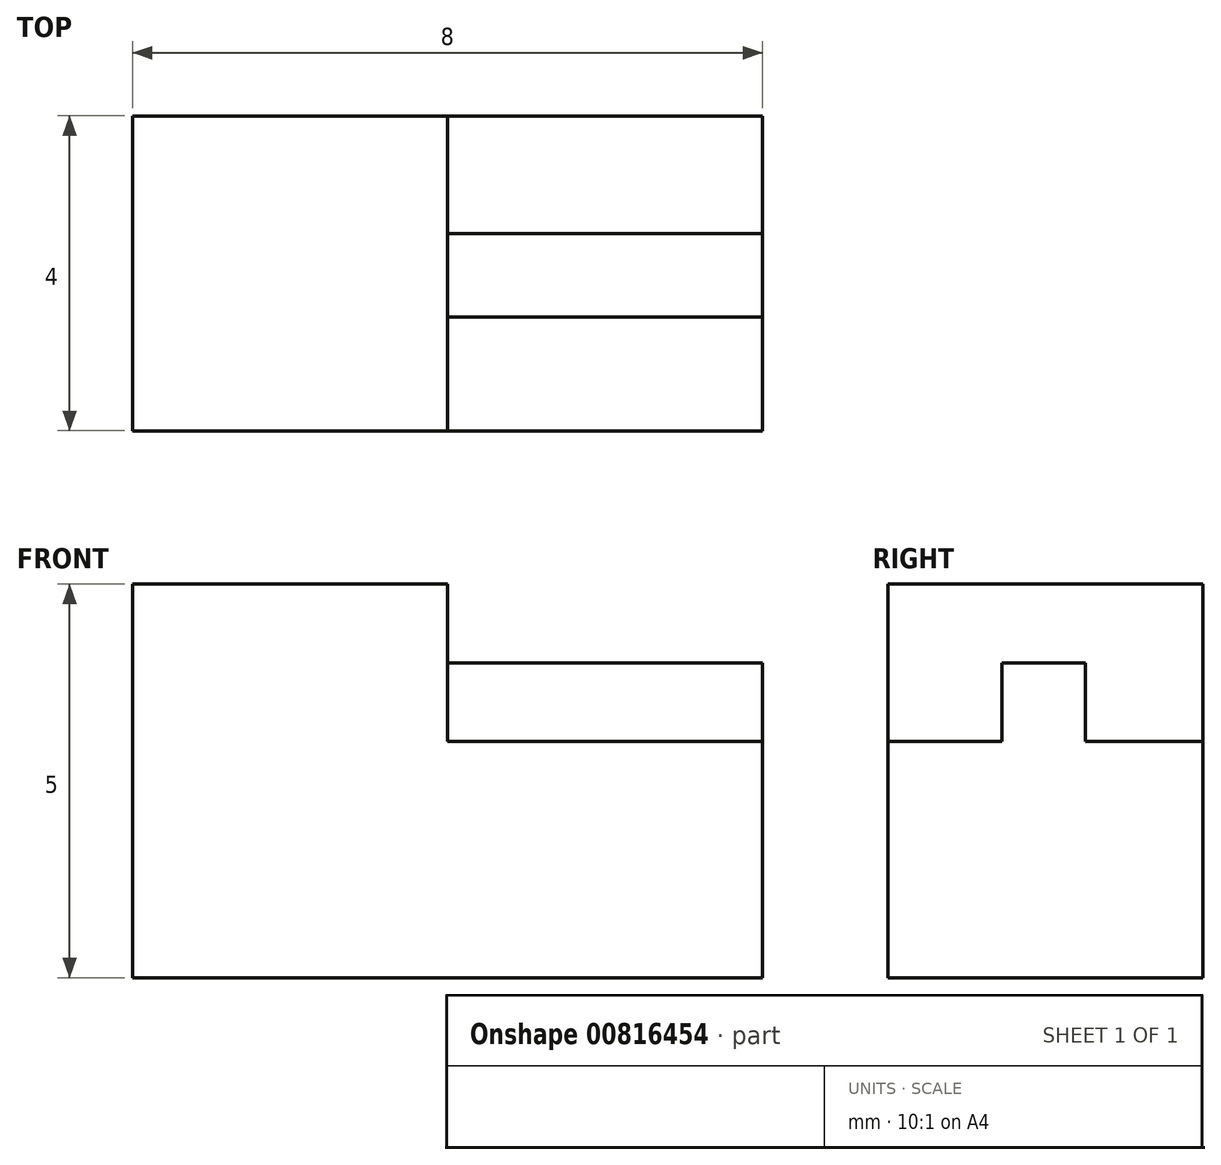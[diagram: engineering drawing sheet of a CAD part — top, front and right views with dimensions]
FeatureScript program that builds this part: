
annotation { "Feature Type Name" : "Feature", "Feature Type Description" : "" }
export const myFeature = defineFeature(function(context is Context, id is Id, definition is map)
    precondition{}
    {
        {
            var Q0;
            Q0=qCreatedBy(makeId("Top.planeOp"),FACE);
            var sketch = newSketch(context, id + "F0", { "sketchPlane" : qUnion([Q0])});
            skLineSegment(sketch, "E0.bottom", {"start": v(-16.71, -4.14) * mm, "end": v(-8.71, -4.14) * mm});
            skLineSegment(sketch, "E0.top", {"start": v(-16.71, -8.14) * mm, "end": v(-8.71, -8.14) * mm});
            skLineSegment(sketch, "E0.left", {"start": v(-16.71, -4.14) * mm, "end": v(-16.71, -8.14) * mm});
            skLineSegment(sketch, "E0.right", {"start": v(-8.71, -4.14) * mm, "end": v(-8.71, -8.14) * mm});
            skPoint(sketch, "E1.visualSharp", {"position": v(-16.71, -4.14) * mm});
            skLineSegment(sketch, "E1.filletArc", {"start": v(-16.71, -4.14) * mm, "end": v(-16.71, -4.14) * mm});
            skPoint(sketch, "E2.visualSharp", {"position": v(-16.71, -8.14) * mm});
            skLineSegment(sketch, "E2.filletArc", {"start": v(-16.71, -8.14) * mm, "end": v(-16.71, -8.14) * mm});
            skSolve(sketch);
        }
        {
            var Q0;
            Q0 = qSketchRegion(id + "F0", true);
            extrude(context, id + "F1", {"entities" : qUnion([Q0]), "depth" : 3 * mm, "offsetDistance" : 25 * mm});
        }
        {
            var Q0;
            Q0=makeQuery(id+"F1.opExtrude","CAP_FACE",FACE,{"disambiguationData":[OSD([sQuery(id+"F0.wireOp",EDGE,"E0.bottom"),sQuery(id+"F0.wireOp",EDGE,"E0.top"),sQuery(id+"F0.wireOp",EDGE,"E0.left"),sQuery(id+"F0.wireOp",EDGE,"E0.right")])],"isStart":false});
            var sketch = newSketch(context, id + "F2", { "sketchPlane" : qUnion([Q0])});
            skLineSegment(sketch, "E3.bottom", {"start": v(-16.71, -8.14) * mm, "end": v(-12.71, -8.14) * mm});
            skLineSegment(sketch, "E3.top", {"start": v(-16.71, -4.14) * mm, "end": v(-12.71, -4.14) * mm});
            skLineSegment(sketch, "E3.left", {"start": v(-16.71, -8.14) * mm, "end": v(-16.71, -4.14) * mm});
            skLineSegment(sketch, "E3.right", {"start": v(-12.71, -8.14) * mm, "end": v(-12.71, -4.14) * mm});
            skSolve(sketch);
        }
        {
            var Q0;
            Q0 = qSketchRegion(id + "F2", true);
            extrude(context, id + "F3", {"entities" : qUnion([Q0]), "operationType" : NewBodyOperationType.ADD, "depth" : 2 * mm, "offsetDistance" : 25 * mm});
        }
        {
            var Q0;
            Q0=makeQuery(id+"F1.opExtrude","CAP_FACE",FACE,{"disambiguationData":[OSD([sQuery(id+"F0.wireOp",EDGE,"E0.bottom"),sQuery(id+"F0.wireOp",EDGE,"E0.top"),sQuery(id+"F0.wireOp",EDGE,"E0.left"),sQuery(id+"F0.wireOp",EDGE,"E0.right")])],"isStart":false});
            var sketch = newSketch(context, id + "F4", { "sketchPlane" : qUnion([Q0])});
            skLineSegment(sketch, "E4.bottom", {"start": v(-12.71, -6.7) * mm, "end": v(-8.71, -6.7) * mm});
            skLineSegment(sketch, "E4.top", {"start": v(-12.71, -5.64) * mm, "end": v(-8.71, -5.64) * mm});
            skLineSegment(sketch, "E4.left", {"start": v(-12.71, -6.7) * mm, "end": v(-12.71, -5.64) * mm});
            skLineSegment(sketch, "E4.right", {"start": v(-8.71, -6.7) * mm, "end": v(-8.71, -5.64) * mm});
            skPoint(sketch, "E5", {"position": v(-12.71, -6.14) * mm});
            skSolve(sketch);
        }
        {
            var Q0;
            Q0 = qSketchRegion(id + "F4", true);
            extrude(context, id + "F5", {"entities" : qUnion([Q0]), "operationType" : NewBodyOperationType.ADD, "depth" : 1 * mm, "offsetDistance" : 25 * mm});
        }
    });
